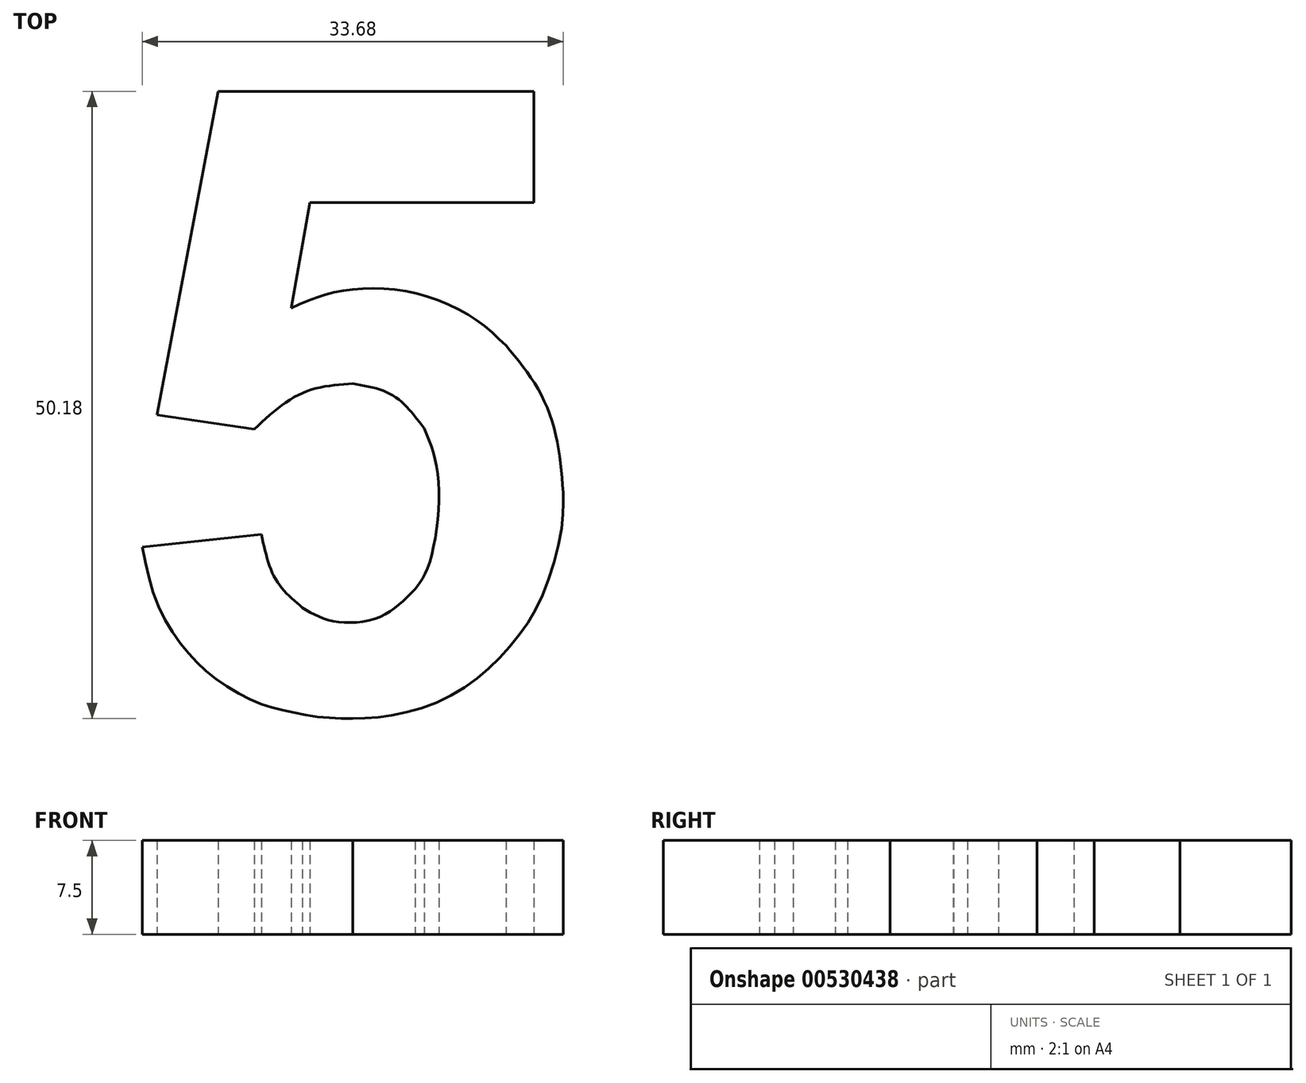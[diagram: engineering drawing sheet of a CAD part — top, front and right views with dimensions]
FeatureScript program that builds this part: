
annotation { "Feature Type Name" : "Feature", "Feature Type Description" : "" }
export const myFeature = defineFeature(function(context is Context, id is Id, definition is map)
    precondition{}
    {
        {
            var Q0;
            Q0=qCreatedBy(makeId("Top.planeOp"),FACE);
            var sketch = newSketch(context, id + "F0", { "sketchPlane" : qUnion([Q0])});
            skLineSegment(sketch, "E0", {"start": v(-10.77, 20.33) * mm, "end": v(14.48, 20.33) * mm});
            skLineSegment(sketch, "E1", {"start": v(14.48, 20.33) * mm, "end": v(14.48, 11.45) * mm});
            skLineSegment(sketch, "E2", {"start": v(14.48, 11.45) * mm, "end": v(-3.44, 11.45) * mm});
            skLineSegment(sketch, "E3", {"start": v(-3.44, 11.45) * mm, "end": v(-4.95, 2.98) * mm});
            skLineSegment(sketch, "E4", {"start": v(-10.77, 20.33) * mm, "end": v(-15.66, -5.55) * mm});
            skLineSegment(sketch, "E5", {"start": v(-15.66, -5.55) * mm, "end": v(-7.9, -6.7) * mm});
            skLineSegment(sketch, "E6", {"start": v(-7.31, -15.12) * mm, "end": v(-16.85, -16.11) * mm});
            skFitSpline(sketch, "E7", {"points": [v(-7.9, -6.7) * mm, v(-4.03, -3.8) * mm, v(0, -3.05) * mm], "startDerivative": vector(7.17, 6.62) * mm, "endDerivative": vector(8.64, 0.58) * mm});
            skFitSpline(sketch, "E8", {"points": [v(0, -3.05) * mm, v(2.41, -3.62) * mm, v(4.1, -4.71) * mm, v(5.7, -6.64) * mm], "startDerivative": vector(7.4, -1.25) * mm, "endDerivative": vector(4.5, -6.02) * mm});
            skFitSpline(sketch, "E9", {"points": [v(5.7, -6.64) * mm, v(6.83, -10.74) * mm, v(6.06, -17.56) * mm, v(4.96, -19.5) * mm], "startDerivative": vector(4.42, -10.72) * mm, "endDerivative": vector(-4.8, -6.17) * mm});
            skFitSpline(sketch, "E10", {"points": [v(4.96, -19.5) * mm, v(2.2, -21.69) * mm, v(-1.65, -22.04) * mm, v(-4.03, -20.97) * mm], "startDerivative": vector(-7.13, -7.47) * mm, "endDerivative": vector(-7.22, 4.4) * mm});
            skFitSpline(sketch, "E11", {"points": [v(-4.03, -20.97) * mm, v(-6.16, -18.72) * mm, v(-7.31, -15.12) * mm], "startDerivative": vector(-5.04, 4.24) * mm, "endDerivative": vector(-1.58, 7.43) * mm});
            skFitSpline(sketch, "E12", {"points": [v(-16.85, -16.11) * mm, v(-15.57, -20.83) * mm, v(-13.43, -24.27) * mm, v(-11.2, -26.46) * mm, v(-8.12, -28.36) * mm, v(-5.63, -29.16) * mm, v(-2.84, -29.7) * mm, v(0, -29.85) * mm], "startDerivative": vector(5.79, -28.55) * mm, "endDerivative": vector(21.65, -0.4) * mm});
            skFitSpline(sketch, "E13", {"points": [v(0, -29.85) * mm, v(2.95, -29.6) * mm, v(7.07, -28.4) * mm, v(10.66, -26.02) * mm, v(13.4, -23.02) * mm, v(15.47, -19.22) * mm, v(16.74, -14.12) * mm, v(16.8, -11.75) * mm], "startDerivative": vector(22.55, 0.82) * mm, "endDerivative": vector(-0.73, 18.9) * mm});
            skFitSpline(sketch, "E14", {"points": [v(16.8, -11.75) * mm, v(16.24, -7.2) * mm, v(14.64, -3.2) * mm, v(12.23, 0) * mm], "startDerivative": vector(-0.97, 13.38) * mm, "endDerivative": vector(-7.97, 9.49) * mm});
            skFitSpline(sketch, "E15", {"points": [v(12.23, 0) * mm, v(10.1, 1.87) * mm, v(7.04, 3.54) * mm, v(3.33, 4.49) * mm, v(0, 4.49) * mm, v(-2.51, 3.98) * mm, v(-4.95, 2.98) * mm], "startDerivative": vector(-12.56, 12.12) * mm, "endDerivative": vector(-15.8, -7.22) * mm});
            skSolve(sketch);
        }
        {
            var Q0;
            Q0=makeQuery(id+"F0.imprint","IMPRINT",FACE,{"disambiguationData":[TD([[makeQuery(id+"F0.imprint","IMPRINT",EDGE,{"derivedFrom":sQuery(id+"F0.wireOp",EDGE,"E0")}),-1.0]])]});
            extrude(context, id + "F1", {"entities" : qUnion([Q0]), "depth" : 7.5 * mm, "offsetDistance" : 25 * mm});
        }
    });
